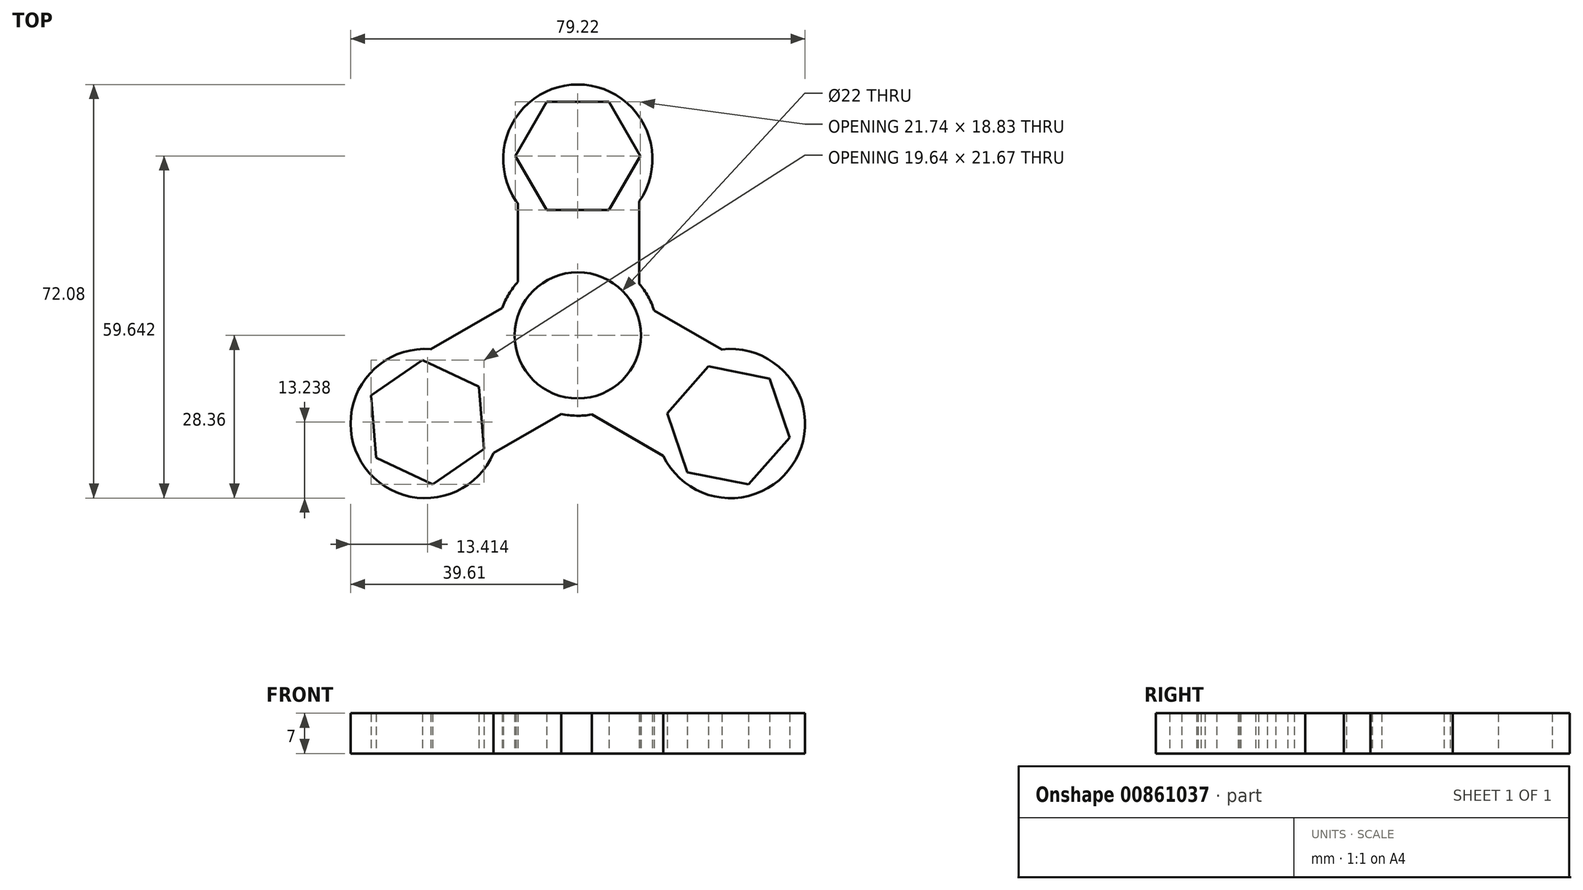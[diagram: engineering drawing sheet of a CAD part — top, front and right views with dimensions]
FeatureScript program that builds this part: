
annotation { "Feature Type Name" : "Feature", "Feature Type Description" : "" }
export const myFeature = defineFeature(function(context is Context, id is Id, definition is map)
    precondition{}
    {
        {
            var Q0;
            Q0=qCreatedBy(makeId("Top.planeOp"),FACE);
            var sketch = newSketch(context, id + "F0", { "sketchPlane" : qUnion([Q0])});
            skCircle(sketch, "E0", {"center": v(0, 0) * mm, "radius": 11 * mm});
            skArc(sketch, "E1", {"start": v(-10.42, 9.35) * mm, "mid": v(-12, 7.2) * mm, "end": v(-13.15, 4.8) * mm});
            skLineSegment(sketch, "E2", {"start": v(0, -11) * mm, "end": v(0, -14) * mm});
            skCircle(sketch, "E3", {"center": v(0, 0) * mm, "radius": 40 * mm, "construction": true});
            skArc(sketch, "E4", {"start": v(10.73, 23.4) * mm, "mid": v(-0.27, 43.72) * mm, "end": v(-10.42, 22.95) * mm});
            skArc(sketch, "E5", {"start": v(-10.42, 22.95) * mm, "mid": v(-10.58, 23.17) * mm, "end": v(-10.73, 23.4) * mm});
            skPoint(sketch, "E6.orphan", {"position": v(9, 24.35) * mm});
            skPoint(sketch, "E7.orphan", {"position": v(-25.59, -4.37) * mm});
            skLineSegment(sketch, "E8", {"start": v(10.73, 23.4) * mm, "end": v(10.73, 8.99) * mm});
            skPoint(sketch, "E9.end.orphan", {"position": v(-10.42, 10.95) * mm});
            skLineSegment(sketch, "E10", {"start": v(-10.42, 22.95) * mm, "end": v(-10.42, 9.35) * mm});
            skArc(sketch, "E11.1.0", {"start": v(-25.63, -2.4) * mm, "mid": v(-37.73, -22.1) * mm, "end": v(-14.67, -20.5) * mm});
            skArc(sketch, "E11.2.0", {"start": v(14.9, -21) * mm, "mid": v(38, -21.63) * mm, "end": v(25.09, -2.45) * mm});
            skLineSegment(sketch, "E12.1.0", {"start": v(-14.67, -20.5) * mm, "end": v(-2.89, -13.7) * mm});
            skLineSegment(sketch, "E12.2.0", {"start": v(25.09, -2.45) * mm, "end": v(13.3, 4.35) * mm});
            skLineSegment(sketch, "E13.1.0", {"start": v(-25.63, -2.4) * mm, "end": v(-13.15, 4.8) * mm});
            skLineSegment(sketch, "E13.2.0", {"start": v(14.9, -21) * mm, "end": v(2.42, -13.79) * mm});
            skArc(sketch, "E14.trimOffspring", {"start": v(13.3, 4.35) * mm, "mid": v(12.24, 6.8) * mm, "end": v(10.73, 8.99) * mm});
            skArc(sketch, "E15.trimOffspring", {"start": v(-2.89, -13.7) * mm, "mid": v(-0.24, -14) * mm, "end": v(2.42, -13.79) * mm});
            skPoint(sketch, "E16.end.orphan", {"position": v(-18.76, 22.95) * mm});
            skSolve(sketch);
        }
        {
            var Q0;
            Q0=makeQuery(id+"F0.imprint","IMPRINT",FACE,{"disambiguationData":[TD([[makeQuery(id+"F0.imprint","IMPRINT",EDGE,{"derivedFrom":sQuery(id+"F0.wireOp",EDGE,"E0")}),-1.0]])]});
            extrude(context, id + "F1", {"entities" : qUnion([Q0]), "depth" : 7 * mm, "offsetDistance" : 25 * mm});
        }
        {
            var Q0;
            Q0=qCreatedBy(makeId("Top.planeOp"),FACE);
            var sketch = newSketch(context, id + "F2", { "sketchPlane" : qUnion([Q0])});
            skCircle(sketch, "E17.cCircle", {"center": v(-26.2, -15.12) * mm, "radius": 9.41 * mm, "construction": true});
            skLineSegment(sketch, "E17.0", {"start": v(-16.37, -19.78) * mm, "end": v(-25.32, -25.96) * mm});
            skLineSegment(sketch, "E17.1", {"start": v(-25.32, -25.96) * mm, "end": v(-35.14, -21.3) * mm});
            skLineSegment(sketch, "E17.2", {"start": v(-35.14, -21.3) * mm, "end": v(-36.02, -10.46) * mm});
            skLineSegment(sketch, "E17.3", {"start": v(-36.02, -10.46) * mm, "end": v(-27.07, -4.29) * mm});
            skLineSegment(sketch, "E17.4", {"start": v(-27.07, -4.29) * mm, "end": v(-17.25, -8.95) * mm});
            skLineSegment(sketch, "E17.5", {"start": v(-17.25, -8.95) * mm, "end": v(-16.37, -19.78) * mm});
            skPoint(sketch, "E17.0.midPoint", {"position": v(-20.85, -22.87) * mm});
            skCircle(sketch, "E18.cCircle", {"center": v(26.24, -15.69) * mm, "radius": 9.41 * mm, "construction": true});
            skLineSegment(sketch, "E18.0", {"start": v(33.4, -7.52) * mm, "end": v(36.9, -17.81) * mm});
            skLineSegment(sketch, "E18.1", {"start": v(36.9, -17.81) * mm, "end": v(29.73, -25.98) * mm});
            skLineSegment(sketch, "E18.2", {"start": v(29.73, -25.98) * mm, "end": v(19.06, -23.86) * mm});
            skLineSegment(sketch, "E18.3", {"start": v(19.06, -23.86) * mm, "end": v(15.57, -13.56) * mm});
            skLineSegment(sketch, "E18.4", {"start": v(15.57, -13.56) * mm, "end": v(22.75, -5.39) * mm});
            skLineSegment(sketch, "E18.5", {"start": v(22.75, -5.39) * mm, "end": v(33.4, -7.52) * mm});
            skPoint(sketch, "E18.0.midPoint", {"position": v(35.15, -12.66) * mm});
            skCircle(sketch, "E19.cCircle", {"center": v(0, 31.28) * mm, "radius": 9.41 * mm, "construction": true});
            skLineSegment(sketch, "E19.0", {"start": v(-5.44, 40.7) * mm, "end": v(5.44, 40.7) * mm});
            skLineSegment(sketch, "E19.1", {"start": v(5.44, 40.7) * mm, "end": v(10.87, 31.28) * mm});
            skLineSegment(sketch, "E19.2", {"start": v(10.87, 31.28) * mm, "end": v(5.44, 21.87) * mm});
            skLineSegment(sketch, "E19.3", {"start": v(5.44, 21.87) * mm, "end": v(-5.44, 21.87) * mm});
            skLineSegment(sketch, "E19.4", {"start": v(-5.44, 21.87) * mm, "end": v(-10.87, 31.28) * mm});
            skLineSegment(sketch, "E19.5", {"start": v(-10.87, 31.28) * mm, "end": v(-5.44, 40.7) * mm});
            skPoint(sketch, "E19.0.midPoint", {"position": v(0, 40.7) * mm});
            skSolve(sketch);
        }
        {
            var Q0;
            Q0 = qSketchRegion(id + "F2", true);
            var Q1;
            Q1=makeQuery(id+"F1.opExtrude","CAP_FACE",FACE,{"disambiguationData":[OSD([sQuery(id+"F0.wireOp",EDGE,"E0"),sQuery(id+"F0.wireOp",EDGE,"E1"),sQuery(id+"F0.wireOp",EDGE,"E4"),sQuery(id+"F0.wireOp",EDGE,"E5"),sQuery(id+"F0.wireOp",EDGE,"E8"),sQuery(id+"F0.wireOp",EDGE,"E10"),sQuery(id+"F0.wireOp",EDGE,"E11.1.0"),sQuery(id+"F0.wireOp",EDGE,"E11.2.0"),sQuery(id+"F0.wireOp",EDGE,"E13.1.0"),sQuery(id+"F0.wireOp",EDGE,"E12.1.0"),sQuery(id+"F0.wireOp",EDGE,"E13.2.0"),sQuery(id+"F0.wireOp",EDGE,"E12.2.0"),sQuery(id+"F0.wireOp",EDGE,"E14.trimOffspring"),sQuery(id+"F0.wireOp",EDGE,"E15.trimOffspring")])],"isStart":false});
            extrude(context, id + "F3", {"entities" : qUnion([Q0, Q1]), "operationType" : NewBodyOperationType.REMOVE, "depth" : 45.5 * mm, "offsetDistance" : 25 * mm});
        }
    });
